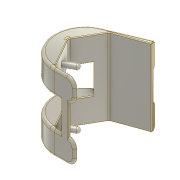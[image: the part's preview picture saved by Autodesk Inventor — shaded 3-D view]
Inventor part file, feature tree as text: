
AUTODESK INVENTOR PART (.ipt)
format: ipt  version: 2017 (Build 210142000, 142)  size: 770,048 bytes
history: native  units: mm
features: other x31, fillet x13, sketch x10, extrude x3, pattern_linear x2
ambient origin geometry x8: Origin, YZ Plane, XZ Plane, XY Plane, X Axis, Y Axis, Z Axis, Center Point
bodies: Body1 (feature_tree)
feature tree (59):
  other  "Bryła1"
  other  "Powierzchnia1"
  other  "Kołnierz1"
  other  "Kołnierz4"
  other  "Kołnierz5"
  other  "Kołnierz6"
  other  "Płaszczyzna konstrukcyjna4"
  other  "Powierzchnia2"
  other  "Kołnierz7"
  sketch  "Szkic13"
  extrude  "Wyciągnięcie proste1"  Depth=2.0mm
  fillet  "Zaokrąglenie1"  Radius=2.0mm
  fillet  "Zaokrąglenie2"  Radius=1.0mm
  other  "Płaszczyzna konstrukcyjna8"
  sketch  "Szkic18"
  extrude  "Wyciągnięcie proste2"  Depth=4.0mm
  pattern_linear  "Szyk prostokątny1"  Spacing1=2.0mm  [1 undecoded]
  extrude  "Wyciągnięcie proste3"  Depth=25.0mm TaperAngle=60.0deg
  pattern_linear  "Szyk prostokątny2"  Spacing1=8.0mm  [1 undecoded]
  other  "Zaokrąglenie narożnika1"
  other  "Zaokrąglenie narożnika2"
  fillet  "Zaokrąglenie3"  Radius=2.0mm
  fillet  "Zaokrąglenie4"  Radius=2.0mm
  fillet  "Zaokrąglenie5"  Radius=2.0mm
  fillet  "Zaokrąglenie6"  Radius=1.0mm
  fillet  "Zaokrąglenie7"  Radius=4.0mm
  fillet  "Zaokrąglenie8"  Radius=2.0mm
  fillet  "Zaokrąglenie9"  Radius=25.0mm
  fillet  "Zaokrąglenie10"  Radius=8.0mm
  fillet  "Zaokrąglenie11"  Radius=2.0mm
  fillet  "Zaokrąglenie12"  Radius=2.0mm
  fillet  "Zaokrąglenie13"  Radius=2.0mm
  sketch  "Szkic1"
  other  "Płyta1"
  sketch  "Szkic2"
  other  "Płyta2"
  other  "Gięcie1"
  other  "Narożnik1"
  sketch  "Szkic5"
  other  "Płyta5"
  other  "Gięcie4"
  other  "Narożnik4"
  sketch  "Szkic8"
  other  "Płyta6"
  other  "Gięcie5"
  other  "Narożnik5"
  sketch  "Szkic9"
  other  "Płyta7"
  other  "Gięcie6"
  other  "Narożnik6"
  sketch  "Szkic11"
  other  "Płyta8"
  other  "Gięcie7"
  sketch  "Szkic12"
  other  "Płyta9"
  other  "Gięcie8"
  other  "Narożnik7"
  sketch  "Szkic14"
  other  "Definicja1"
note: 2 required parameter values undecoded (feature->parameter linkage not recoverable at this tier; creation-order binding heuristic only, values carry confidence <= 0.55)
